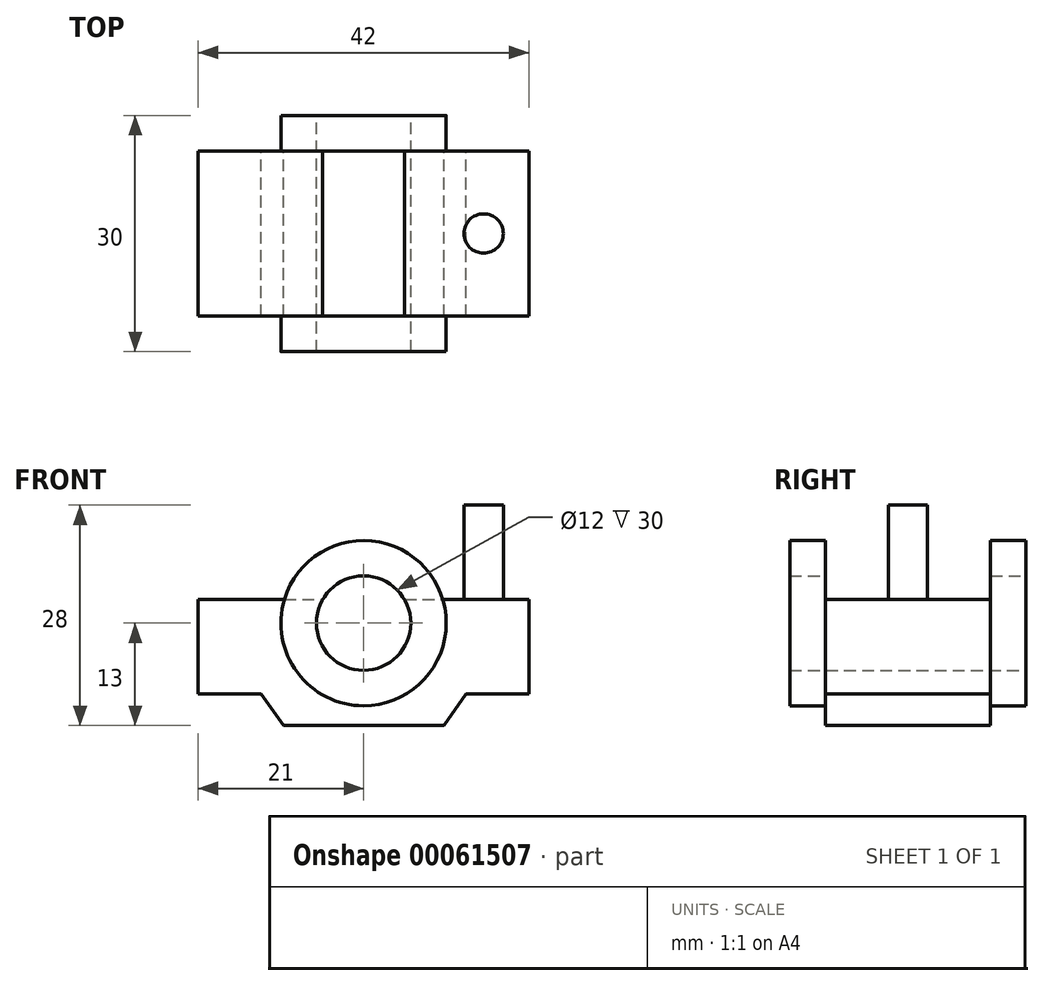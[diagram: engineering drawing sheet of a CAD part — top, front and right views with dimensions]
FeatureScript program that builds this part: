
annotation { "Feature Type Name" : "Feature", "Feature Type Description" : "" }
export const myFeature = defineFeature(function(context is Context, id is Id, definition is map)
    precondition{}
    {
        {
            var Q0;
            Q0=qCreatedBy(makeId("Front.planeOp"),FACE);
            var sketch = newSketch(context, id + "F0", { "sketchPlane" : qUnion([Q0])});
            skCircle(sketch, "E0", {"center": v(0, 0) * mm, "radius": 10.5 * mm});
            skCircle(sketch, "E1", {"center": v(0, 0) * mm, "radius": 6 * mm});
            skLineSegment(sketch, "E2", {"start": v(0, 15) * mm, "end": v(-21, 15) * mm});
            skLineSegment(sketch, "E3.MirrorCS", {"start": v(0, 15) * mm, "end": v(21, 15) * mm});
            skLineSegment(sketch, "E4", {"start": v(-21, 15) * mm, "end": v(-21, -9) * mm});
            skLineSegment(sketch, "E5.MirrorCS", {"start": v(21, 15) * mm, "end": v(21, -9) * mm});
            skLineSegment(sketch, "E6", {"start": v(-21, -9) * mm, "end": v(-13, -9) * mm});
            skLineSegment(sketch, "E7.MirrorCS", {"start": v(21, -9) * mm, "end": v(13, -9) * mm});
            skLineSegment(sketch, "E8", {"start": v(-13, -9) * mm, "end": v(-10.2, -13) * mm});
            skLineSegment(sketch, "E9", {"start": v(-10.2, -13) * mm, "end": v(10.2, -13) * mm});
            skLineSegment(sketch, "E10", {"start": v(10.2, -13) * mm, "end": v(13, -9) * mm});
            skSolve(sketch);
        }
        {
            var Q0;
            Q0=makeQuery(id+"F0.imprint","IMPRINT",FACE,{"disambiguationData":[TD([[makeQuery(id+"F0.imprint","IMPRINT",EDGE,{"derivedFrom":sQuery(id+"F0.wireOp",EDGE,"E0")}),1.0]])]});
            extrude(context, id + "F1", {"entities" : qUnion([Q0]), "depth" : 30 * mm, "symmetric" : true});
        }
        {
            var Q0;
            Q0=makeQuery(id+"F0.imprint","IMPRINT",FACE,{"disambiguationData":[TD([[makeQuery(id+"F0.imprint","IMPRINT",EDGE,{"derivedFrom":sQuery(id+"F0.wireOp",EDGE,"E0")}),-1.0]])]});
            extrude(context, id + "F2", {"entities" : qUnion([Q0]), "operationType" : NewBodyOperationType.ADD, "depth" : 21 * mm, "symmetric" : true});
        }
        {
            var Q0;
            Q0=makeQuery(id+"F2.opExtrude","SWEPT_FACE",FACE,{"disambiguationData":[OSD([sQuery(id+"F0.wireOp",EDGE,"E2"),sQuery(id+"F0.wireOp",EDGE,"E3.MirrorCS")])]});
            var sketch = newSketch(context, id + "F3", { "sketchPlane" : qUnion([Q0])});
            skCircle(sketch, "E11", {"center": v(-15.25, 0) * mm, "radius": 2.5 * mm});
            skCircle(sketch, "E12.MirrorC", {"center": v(15.25, 0) * mm, "radius": 2.5 * mm});
            skSolve(sketch);
        }
        {
            var Q0;
            Q0=makeQuery(id+"F3.imprint","IMPRINT",FACE,{"disambiguationData":[TD([[makeQuery(id+"F3.imprint","IMPRINT",EDGE,{"derivedFrom":sQuery(id+"F3.wireOp",EDGE,"E11")}),1.0]])]});
            var Q1;
            Q1=makeQuery(id+"F3.imprint","IMPRINT",FACE,{"disambiguationData":[TD([[makeQuery(id+"F3.imprint","IMPRINT",EDGE,{"derivedFrom":sQuery(id+"F3.wireOp",EDGE,"E12.MirrorC")}),-1.0]])]});
            extrude(context, id + "F4", {"entities" : qUnion([Q0, Q1]), "operationType" : NewBodyOperationType.REMOVE, "oppositeDirection" : true, "depth" : 12 * mm});
        }
    });
